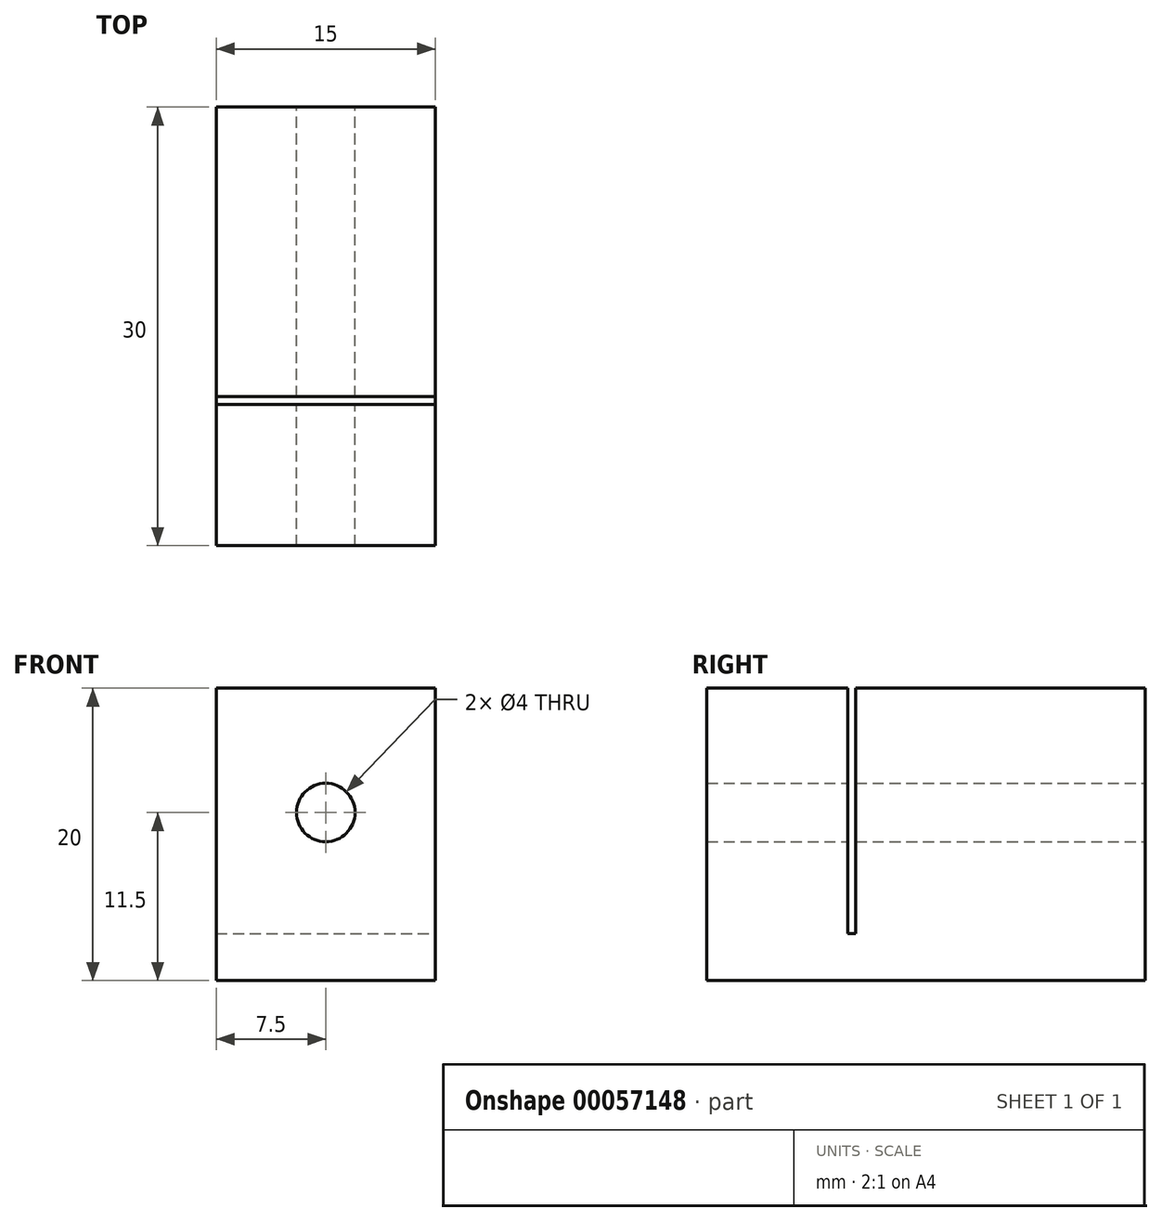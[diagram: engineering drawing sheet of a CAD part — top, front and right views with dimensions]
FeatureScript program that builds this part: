
annotation { "Feature Type Name" : "Feature", "Feature Type Description" : "" }
export const myFeature = defineFeature(function(context is Context, id is Id, definition is map)
    precondition{}
    {
        {
            var Q0;
            Q0=qCreatedBy(makeId("Front.planeOp"),FACE);
            var sketch = newSketch(context, id + "F0", { "sketchPlane" : qUnion([Q0])});
            skCircle(sketch, "E0", {"center": v(0, 0) * mm, "radius": 2 * mm});
            skLineSegment(sketch, "E1.bottom", {"start": v(-7.5, 8.5) * mm, "end": v(7.5, 8.5) * mm});
            skLineSegment(sketch, "E1.top", {"start": v(-7.5, -11.5) * mm, "end": v(7.5, -11.5) * mm});
            skLineSegment(sketch, "E1.left", {"start": v(-7.5, 8.5) * mm, "end": v(-7.5, -11.5) * mm});
            skLineSegment(sketch, "E1.right", {"start": v(7.5, 8.5) * mm, "end": v(7.5, -11.5) * mm});
            skSolve(sketch);
        }
        {
            var Q0;
            Q0 = qSketchRegion(id + "F0", true);
            extrude(context, id + "F1", {"entities" : qUnion([Q0]), "depth" : 30 * mm});
        }
        {
            var Q0;
            Q0=makeQuery(id+"F1.opExtrude","SWEPT_FACE",FACE,{"disambiguationData":[OSD([sQuery(id+"F0.wireOp",EDGE,"E1.right")])]});
            var sketch = newSketch(context, id + "F2", { "sketchPlane" : qUnion([Q0])});
            skLineSegment(sketch, "E2.0", {"start": v(-30, -2) * mm, "end": v(-30, 2) * mm, "construction": true});
            skLineSegment(sketch, "E3.0", {"start": v(-30, 8.5) * mm, "end": v(0, 8.5) * mm, "construction": true});
            skLineSegment(sketch, "E4.bottom", {"start": v(-20.35, 8.5) * mm, "end": v(-19.8, 8.5) * mm});
            skLineSegment(sketch, "E4.top", {"start": v(-20.35, -8.27) * mm, "end": v(-19.8, -8.27) * mm});
            skLineSegment(sketch, "E4.left", {"start": v(-20.35, 8.5) * mm, "end": v(-20.35, -8.27) * mm});
            skLineSegment(sketch, "E4.right", {"start": v(-19.8, 8.5) * mm, "end": v(-19.8, -8.27) * mm});
            skSolve(sketch);
        }
        {
            var Q0;
            Q0 = qSketchRegion(id + "F2", true);
            var Q1;
            Q1=makeQuery(id+"F1.opExtrude","SWEPT_FACE",FACE,{"disambiguationData":[OSD([sQuery(id+"F0.wireOp",EDGE,"E1.left")])]});
            extrude(context, id + "F3", {"entities" : qUnion([Q0]), "operationType" : NewBodyOperationType.REMOVE, "endBound" : BoundingType.UP_TO_SURFACE, "oppositeDirection" : true, "endBoundEntityFace" : qUnion([Q1]), "depth" : 25 * mm});
        }
    });
